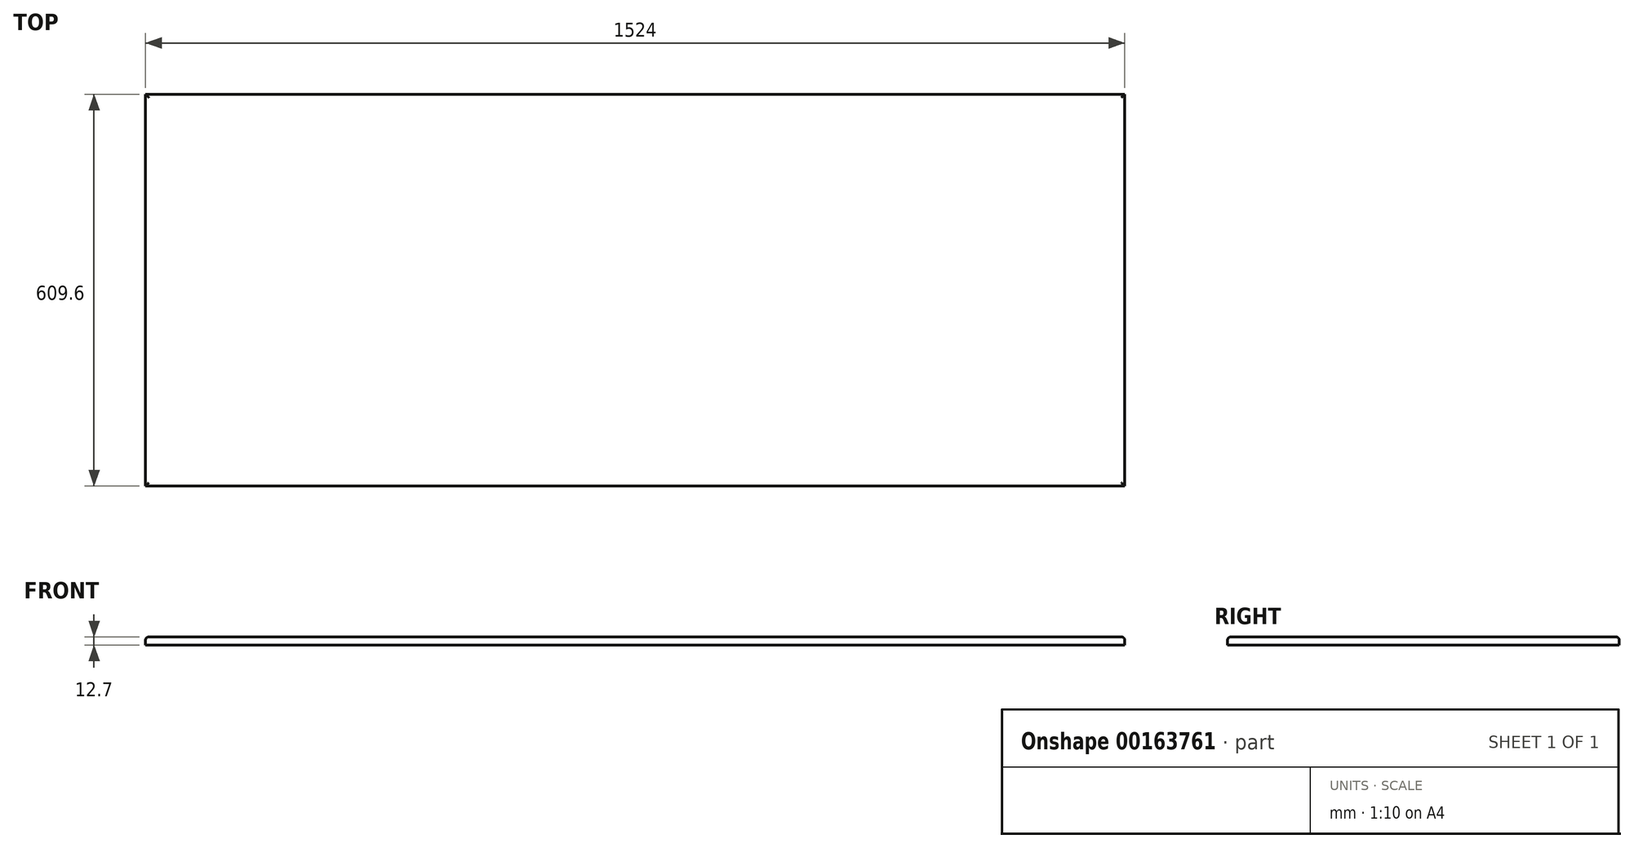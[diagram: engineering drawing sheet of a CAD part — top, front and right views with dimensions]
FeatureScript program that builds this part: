
annotation { "Feature Type Name" : "Feature", "Feature Type Description" : "" }
export const myFeature = defineFeature(function(context is Context, id is Id, definition is map)
    precondition{}
    {
        {
            var Q0;
            Q0=qCreatedBy(makeId("Top.planeOp"),FACE);
            var sketch = newSketch(context, id + "F0", { "sketchPlane" : qUnion([Q0])});
            skLineSegment(sketch, "E0.bottom", {"start": v(762, 304.8) * mm, "end": v(-762, 304.8) * mm});
            skLineSegment(sketch, "E0.top", {"start": v(762, -304.8) * mm, "end": v(-762, -304.8) * mm});
            skLineSegment(sketch, "E0.left", {"start": v(762, 304.8) * mm, "end": v(762, -304.8) * mm});
            skLineSegment(sketch, "E0.right", {"start": v(-762, 304.8) * mm, "end": v(-762, -304.8) * mm});
            skPoint(sketch, "E0.middle", {"position": v(0, 0) * mm});
            skSolve(sketch);
        }
        {
            var Q0;
            Q0 = qSketchRegion(id + "F0", true);
            extrude(context, id + "F1", {"entities" : qUnion([Q0]), "depth" : 12.7 * mm});
        }
        {
            var Q0;
            Q0=makeQuery(id+"F1.opExtrude","CAP_FACE",FACE,{"disambiguationData":[OSD([sQuery(id+"F0.wireOp",EDGE,"E0.bottom"),sQuery(id+"F0.wireOp",EDGE,"E0.top"),sQuery(id+"F0.wireOp",EDGE,"E0.left"),sQuery(id+"F0.wireOp",EDGE,"E0.right")])],"isStart":false});
            fillet(context, id + "F2", {"entities" : qUnion([Q0]), "radius" : 5.08 * mm, "tangentPropagation" : true, "allowEdgeOverflow" : false});
        }
    });
